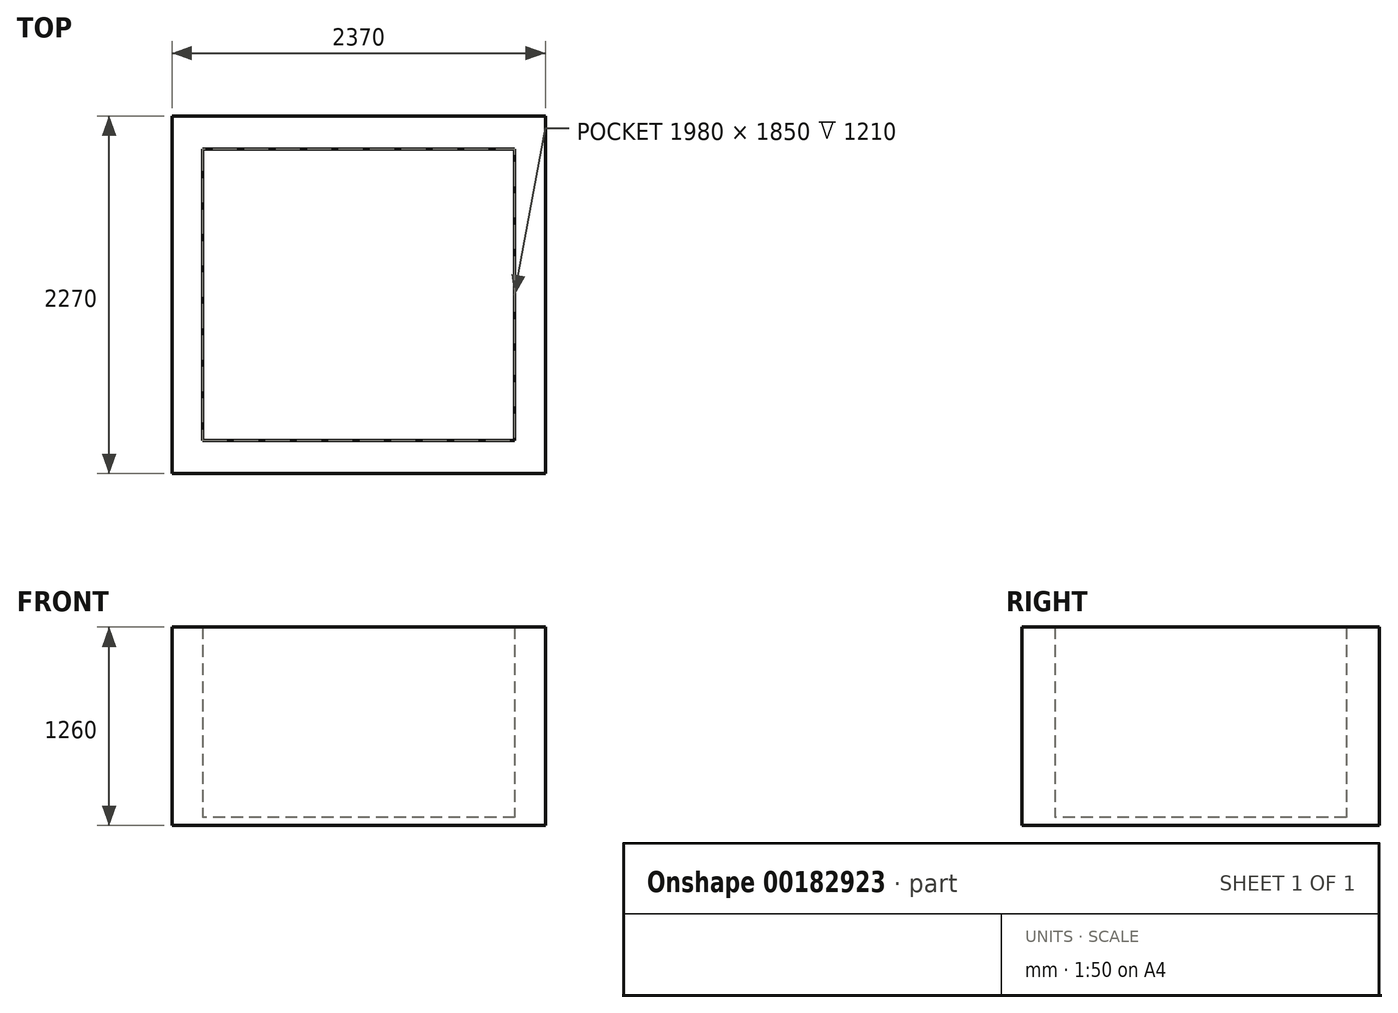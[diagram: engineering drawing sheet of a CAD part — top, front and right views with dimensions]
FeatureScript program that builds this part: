
annotation { "Feature Type Name" : "Feature", "Feature Type Description" : "" }
export const myFeature = defineFeature(function(context is Context, id is Id, definition is map)
    precondition{}
    {
        {
            var Q0;
            Q0=qCreatedBy(makeId("Top.planeOp"),FACE);
            var sketch = newSketch(context, id + "F0", { "sketchPlane" : qUnion([Q0])});
            skLineSegment(sketch, "E0.bottom", {"start": v(990, 925) * mm, "end": v(-990, 925) * mm});
            skLineSegment(sketch, "E0.top", {"start": v(990, -925) * mm, "end": v(-990, -925) * mm});
            skLineSegment(sketch, "E0.left", {"start": v(990, 925) * mm, "end": v(990, -925) * mm});
            skLineSegment(sketch, "E0.right", {"start": v(-990, 925) * mm, "end": v(-990, -925) * mm});
            skPoint(sketch, "E0.middle", {"position": v(0, 0) * mm});
            skLineSegment(sketch, "E1.bottom", {"start": v(1185, 1135) * mm, "end": v(-1185, 1135) * mm});
            skLineSegment(sketch, "E1.top", {"start": v(1185, -1135) * mm, "end": v(-1185, -1135) * mm});
            skLineSegment(sketch, "E1.left", {"start": v(1185, 1135) * mm, "end": v(1185, -1135) * mm});
            skLineSegment(sketch, "E1.right", {"start": v(-1185, 1135) * mm, "end": v(-1185, -1135) * mm});
            skSolve(sketch);
        }
        {
            var Q0;
            Q0=makeQuery(id+"F0.imprint","IMPRINT",FACE,{"disambiguationData":[TD([[makeQuery(id+"F0.imprint","IMPRINT",EDGE,{"derivedFrom":sQuery(id+"F0.wireOp",EDGE,"E0.bottom")}),1.0]])]});
            extrude(context, id + "F1", {"entities" : qUnion([Q0]), "depth" : 50 * mm});
        }
        {
            var Q0;
            Q0 = qSketchRegion(id + "F0", true);
            extrude(context, id + "F2", {"entities" : qUnion([Q0]), "operationType" : NewBodyOperationType.ADD, "depth" : 1260 * mm});
        }
    });
